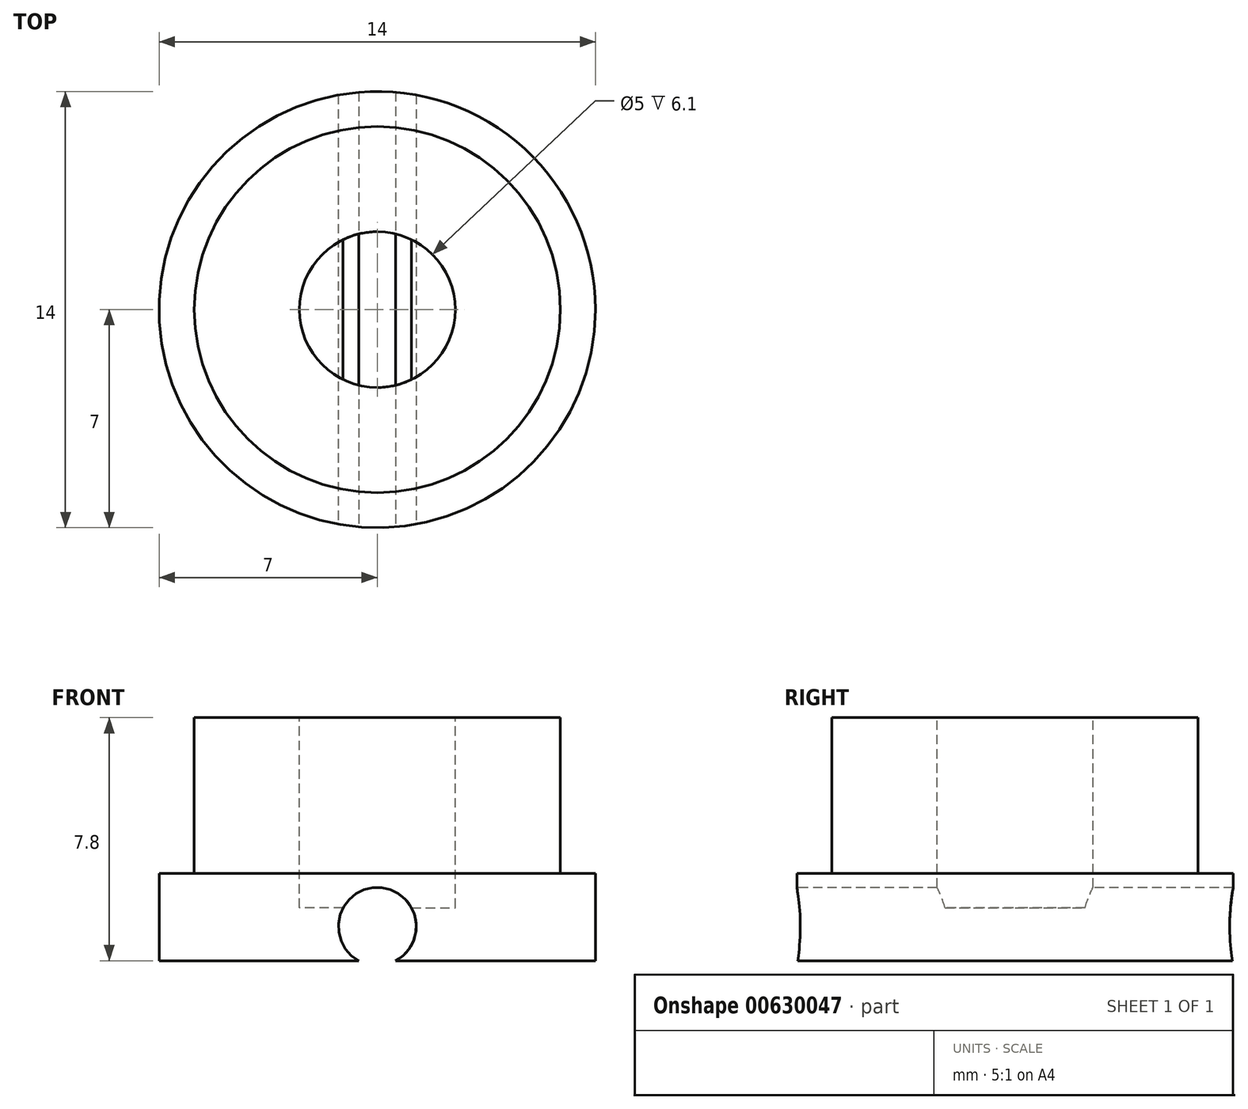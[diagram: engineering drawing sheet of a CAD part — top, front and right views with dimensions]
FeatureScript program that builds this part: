
annotation { "Feature Type Name" : "Feature", "Feature Type Description" : "" }
export const myFeature = defineFeature(function(context is Context, id is Id, definition is map)
    precondition{}
    {
        {
            var Q0;
            Q0=qCreatedBy(makeId("Top.planeOp"),FACE);
            var sketch = newSketch(context, id + "F0", { "sketchPlane" : qUnion([Q0])});
            skCircle(sketch, "E0", {"center": v(0, 0) * mm, "radius": 7 * mm});
            skSolve(sketch);
        }
        {
            var Q0;
            Q0=makeQuery(id+"F0.imprint","IMPRINT",FACE,{"disambiguationData":[TD([[makeQuery(id+"F0.imprint","IMPRINT",EDGE,{"derivedFrom":sQuery(id+"F0.wireOp",EDGE,"E0")}),1.0]])]});
            extrude(context, id + "F1", {"entities" : qUnion([Q0]), "depth" : 2.8 * mm, "offsetDistance" : 25 * mm});
        }
        {
            var Q0;
            Q0=makeQuery(id+"F1.opExtrude","CAP_FACE",FACE,{"disambiguationData":[OSD([sQuery(id+"F0.wireOp",EDGE,"E0")])],"isStart":false});
            var sketch = newSketch(context, id + "F2", { "sketchPlane" : qUnion([Q0])});
            skCircle(sketch, "E1", {"center": v(0, 0) * mm, "radius": 5.88 * mm});
            skSolve(sketch);
        }
        {
            var Q0;
            Q0=makeQuery(id+"F2.imprint","IMPRINT",FACE,{"disambiguationData":[TD([[makeQuery(id+"F2.imprint","IMPRINT",EDGE,{"derivedFrom":sQuery(id+"F2.wireOp",EDGE,"E1")}),1.0]])]});
            extrude(context, id + "F3", {"entities" : qUnion([Q0]), "operationType" : NewBodyOperationType.ADD, "depth" : 5 * mm, "offsetDistance" : 25 * mm});
        }
        {
            var Q0;
            Q0=qCreatedBy(makeId("Front.planeOp"),FACE);
            var sketch = newSketch(context, id + "F4", { "sketchPlane" : qUnion([Q0])});
            skCircle(sketch, "E2", {"center": v(0, 1.1) * mm, "radius": 1.25 * mm});
            skSolve(sketch);
        }
        {
            var Q0;
            Q0=makeQuery(id+"F4.imprint","IMPRINT",FACE,{"disambiguationData":[TD([[makeQuery(id+"F4.imprint","IMPRINT",EDGE,{"derivedFrom":sQuery(id+"F4.wireOp",EDGE,"E2")}),1.0]])]});
            extrude(context, id + "F5", {"entities" : qUnion([Q0]), "operationType" : NewBodyOperationType.REMOVE, "endBound" : BoundingType.THROUGH_ALL, "oppositeDirection" : true, "depth" : 25 * mm, "offsetDistance" : 25 * mm, "hasSecondDirection" : true, "secondDirectionBound" : SecondDirectionBoundingType.THROUGH_ALL, "secondDirectionOppositeDirection" : false, "secondDirectionDepth" : 25 * mm});
        }
        {
            var Q0;
            Q0=makeQuery(id+"F3.opExtrude","CAP_FACE",FACE,{"disambiguationData":[OSD([sQuery(id+"F2.wireOp",EDGE,"E1")])],"isStart":false});
            var sketch = newSketch(context, id + "F6", { "sketchPlane" : qUnion([Q0])});
            skCircle(sketch, "E3", {"center": v(0, 0) * mm, "radius": 2.5 * mm});
            skSolve(sketch);
        }
        {
            var Q0;
            Q0=makeQuery(id+"F6.imprint","IMPRINT",FACE,{"disambiguationData":[TD([[makeQuery(id+"F6.imprint","IMPRINT",EDGE,{"derivedFrom":sQuery(id+"F6.wireOp",EDGE,"E3")}),1.0]])]});
            var Q1;
            Q1=makeQuery(id+"F5.boolean.opBoolean","SPLIT",FACE,{"disambiguationData":[OD(1.0)],"derivedFrom":makeQuery(id+"F1.opExtrude","CAP_FACE",FACE,{"disambiguationData":[OSD([sQuery(id+"F0.wireOp",EDGE,"E0")])],"isStart":true})});
            extrude(context, id + "F7", {"entities" : qUnion([Q0]), "operationType" : NewBodyOperationType.REMOVE, "endBound" : BoundingType.UP_TO_SURFACE, "oppositeDirection" : true, "depth" : 25 * mm, "endBoundEntityFace" : qUnion([Q1]), "hasOffset" : true, "offsetDistance" : 1.7 * mm});
        }
    });
